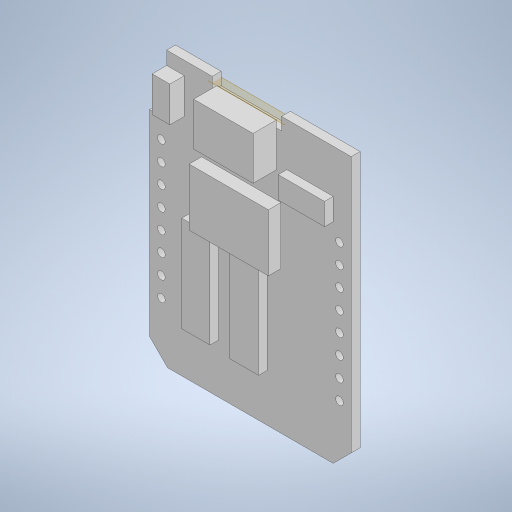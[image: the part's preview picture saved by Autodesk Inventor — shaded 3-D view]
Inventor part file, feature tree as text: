
AUTODESK INVENTOR PART (.ipt)
format: ipt  version: 2023 (Build 270158000, 158)  size: 366,080 bytes
history: native  units: mm
features: extrude x8, sketch x6, plane x1, projected_geometry x1
ambient origin geometry x8: Origin, YZ Plane, XZ Plane, XY Plane, X Axis, Y Axis, Z Axis, Center Point
bodies: Body1 (feature_tree)
feature tree (16):
  extrude  "Extrusion2"  Depth=35.0mm
  plane  "Work Plane1"
  extrude  "Extrusion3"  Depth=7.65mm
  extrude  "Extrusion4"  Depth=8.88mm
  extrude  "Extrusion5"  Depth=1.0mm
  sketch  "Sketch5"  dims[d11=1.5mm d12=7.3mm]
  extrude  "Extrusion6"  Depth=7.3mm
  extrude  "Extrusion7"  Depth=2.3mm
  extrude  "Extrusion8"  Depth=2.3mm
  extrude  "Extrusion9"  Depth=1.13mm TaperAngle=0.0deg
  sketch  "Sketch1"  dims[d0=25.7mm d1=35.0mm]
  sketch  "Sketch2"  dims[d4=2.18mm d5=7.65mm]
  projected_geometry  "Projected Loop1"
  sketch  "Sketch3"  dims[d7=5.8mm d8=8.88mm]
  sketch  "Sketch4"  dims[d9=1.6mm d10=1.0mm]
  sketch  "Sketch6"  dims[d13=80.0mm d15=2.5mm d16=10.0mm d18=10.0mm d20=2.3mm d21=2.3mm d22=1.13mm d23=0.0mm d24=0.9mm d25=7.57mm d26=3.0mm d27=0.0mm d28=0.0mm d29=5.5mm d30=0.0mm d31=10.55mm d32=16.0mm d33=5.1mm d34=0.5mm d35=1.0mm d36=0.0mm d37=12.0mm d38=15.1mm d39=7.8mm d40=2.0mm d41=2.3mm d42=0.0mm d43=1.7mm d44=2.25mm d45=4.5mm d46=6.31mm d47=3.6mm d48=5.2mm d49=12.2mm d50=6.64mm d51=7.29mm d52=18.66mm d53=6.56mm d54=11.66mm d55=3.7mm d56=15.0mm d57=10.1mm d58=1.85mm d59=0.0mm d60=1.1mm d61=0.0mm d62=1.6mm d63=0.0mm d64=3.0mm d65=5.76mm d66=1.7mm d67=0.5mm d68=0.65mm d69=0.0mm]
